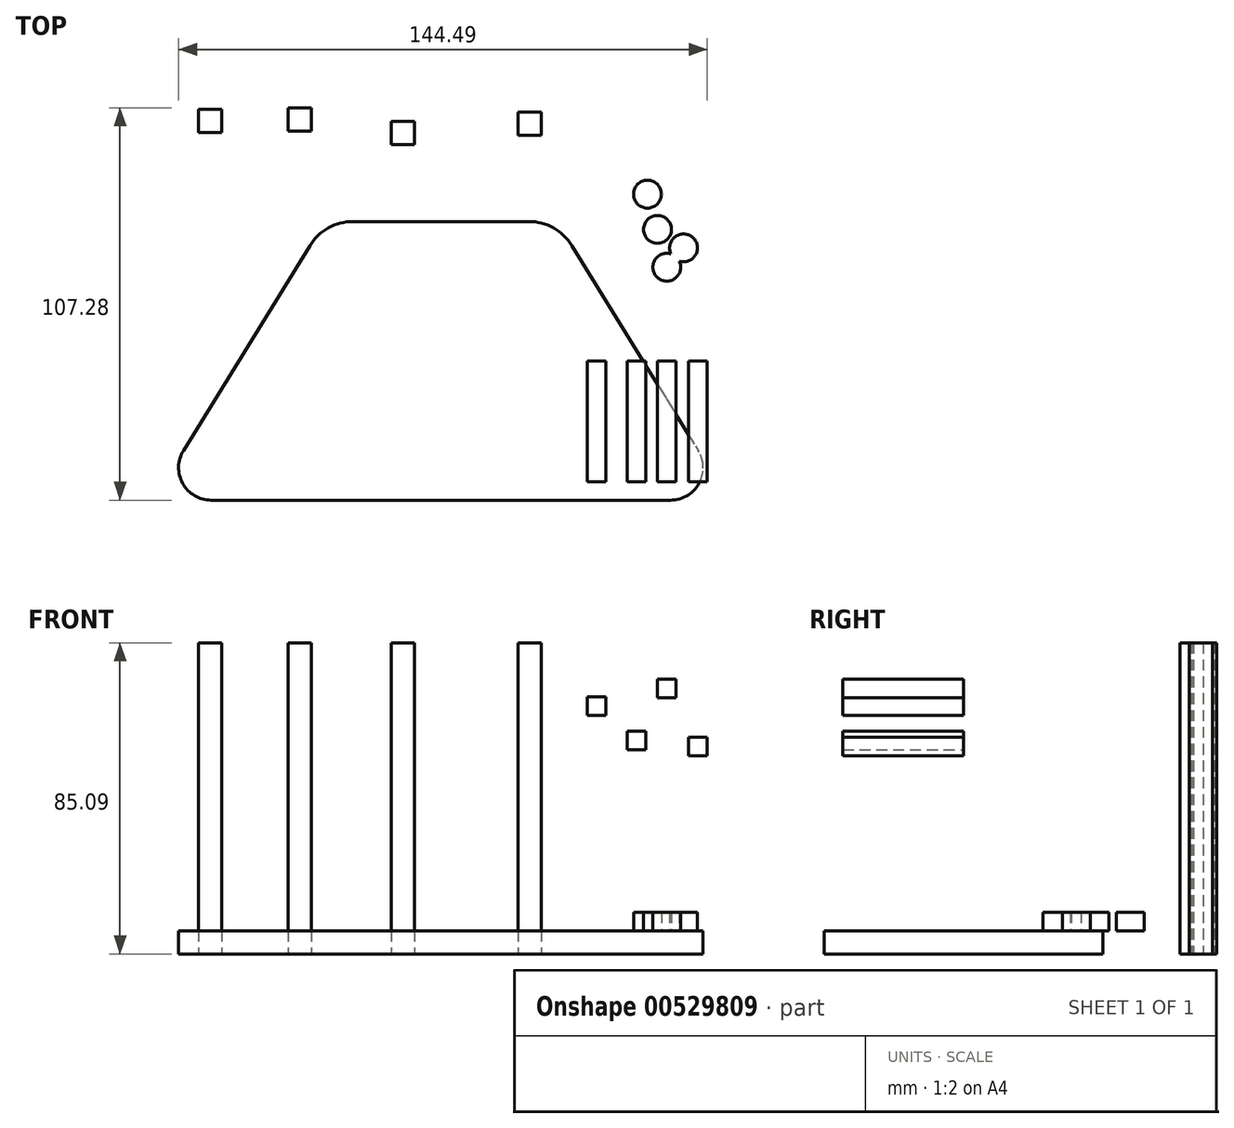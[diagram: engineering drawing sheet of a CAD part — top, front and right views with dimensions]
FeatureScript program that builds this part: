
annotation { "Feature Type Name" : "Feature", "Feature Type Description" : "" }
export const myFeature = defineFeature(function(context is Context, id is Id, definition is map)
    precondition{}
    {
        {
            var Q0;
            Q0=qCreatedBy(makeId("Top.planeOp"),FACE);
            var sketch = newSketch(context, id + "F0", { "sketchPlane" : qUnion([Q0])});
            skLineSegment(sketch, "E0.bottom", {"start": v(-23.95, 38.1) * mm, "end": v(23.95, 38.1) * mm});
            skLineSegment(sketch, "E0.top", {"start": v(-31.75, -38.1) * mm, "end": v(31.75, -38.1) * mm});
            skLineSegment(sketch, "E0.left", {"start": v(-31.75, 38.1) * mm, "end": v(-31.75, -38.1) * mm});
            skLineSegment(sketch, "E0.right", {"start": v(31.75, 38.1) * mm, "end": v(31.75, -38.1) * mm});
            skPoint(sketch, "E0.middle", {"position": v(0, 0) * mm});
            skLineSegment(sketch, "E1", {"start": v(-31.75, -38.1) * mm, "end": v(-62.81, -38.1) * mm});
            skLineSegment(sketch, "E2", {"start": v(31.75, -38.1) * mm, "end": v(62.81, -38.1) * mm});
            skLineSegment(sketch, "E3", {"start": v(-70.38, -24.54) * mm, "end": v(-35.84, 31.46) * mm});
            skLineSegment(sketch, "E4", {"start": v(35.84, 31.46) * mm, "end": v(70.38, -24.54) * mm});
            skPoint(sketch, "E5.visualSharp", {"position": v(-31.75, 38.1) * mm});
            skArc(sketch, "E5.filletArc", {"start": v(-23.95, 38.1) * mm, "mid": v(-30.76, 36.33) * mm, "end": v(-35.84, 31.46) * mm});
            skPoint(sketch, "E6.visualSharp", {"position": v(31.75, 38.1) * mm});
            skArc(sketch, "E6.filletArc", {"start": v(35.84, 31.46) * mm, "mid": v(30.76, 36.33) * mm, "end": v(23.95, 38.1) * mm});
            skPoint(sketch, "E7.visualSharp", {"position": v(78.74, -38.1) * mm});
            skArc(sketch, "E7.filletArc", {"start": v(62.81, -38.1) * mm, "mid": v(70.58, -33.54) * mm, "end": v(70.38, -24.54) * mm});
            skPoint(sketch, "E8.visualSharp", {"position": v(-78.74, -38.1) * mm});
            skArc(sketch, "E8.filletArc", {"start": v(-70.38, -24.54) * mm, "mid": v(-70.58, -33.54) * mm, "end": v(-62.81, -38.1) * mm});
            skSolve(sketch);
        }
        {
            var Q0;
            {var subQ7=sQuery(id+"F0.wireOp",EDGE,"E0.bottom");Q0=makeQuery(id+"F0.imprint","IMPRINT",FACE,{"disambiguationData":[TD([[makeQuery(id+"F0.imprint","IMPRINT",EDGE,{"derivedFrom":subQ7}),-1.0]])]});}
            var Q1;
            {var subQ4=sQuery(id+"F0.wireOp",EDGE,"E1");Q1=makeQuery(id+"F0.imprint","IMPRINT",FACE,{"disambiguationData":[TD([[makeQuery(id+"F0.imprint","IMPRINT",EDGE,{"derivedFrom":subQ4}),-1.0]])]});}
            var Q2;
            {var subQ4=sQuery(id+"F0.wireOp",EDGE,"E2");Q2=makeQuery(id+"F0.imprint","IMPRINT",FACE,{"disambiguationData":[TD([[makeQuery(id+"F0.imprint","IMPRINT",EDGE,{"derivedFrom":subQ4}),1.0]])]});}
            extrude(context, id + "F1", {"entities" : qUnion([Q0, Q1, Q2]), "depth" : 6.35 * mm, "offsetDistance" : 25.4 * mm});
        }
        {
            var Q0;
            Q0=qCreatedBy(makeId("Top.planeOp"),FACE);
            var sketch = newSketch(context, id + "F2", { "sketchPlane" : qUnion([Q0])});
            skLineSegment(sketch, "E9.bottom", {"start": v(-59.93, 62.37) * mm, "end": v(-66.28, 62.37) * mm});
            skLineSegment(sketch, "E9.top", {"start": v(-59.93, 68.72) * mm, "end": v(-66.28, 68.72) * mm});
            skLineSegment(sketch, "E9.left", {"start": v(-59.93, 62.37) * mm, "end": v(-59.93, 68.72) * mm});
            skLineSegment(sketch, "E9.right", {"start": v(-66.28, 62.37) * mm, "end": v(-66.28, 68.72) * mm});
            skPoint(sketch, "E9.middle", {"position": v(-63.1, 65.55) * mm});
            skLineSegment(sketch, "E10.bottom", {"start": v(-35.4, 62.83) * mm, "end": v(-41.75, 62.83) * mm});
            skLineSegment(sketch, "E10.top", {"start": v(-35.4, 69.18) * mm, "end": v(-41.75, 69.18) * mm});
            skLineSegment(sketch, "E10.left", {"start": v(-35.4, 62.83) * mm, "end": v(-35.4, 69.18) * mm});
            skLineSegment(sketch, "E10.right", {"start": v(-41.75, 62.83) * mm, "end": v(-41.75, 69.18) * mm});
            skPoint(sketch, "E10.middle", {"position": v(-38.57, 66) * mm});
            skLineSegment(sketch, "E11.bottom", {"start": v(-7.16, 59.16) * mm, "end": v(-13.5, 59.16) * mm});
            skLineSegment(sketch, "E11.top", {"start": v(-7.16, 65.5) * mm, "end": v(-13.5, 65.5) * mm});
            skLineSegment(sketch, "E11.left", {"start": v(-7.16, 59.16) * mm, "end": v(-7.16, 65.5) * mm});
            skLineSegment(sketch, "E11.right", {"start": v(-13.5, 59.16) * mm, "end": v(-13.5, 65.5) * mm});
            skPoint(sketch, "E11.middle", {"position": v(-10.33, 62.33) * mm});
            skLineSegment(sketch, "E12.bottom", {"start": v(27.51, 61.68) * mm, "end": v(21.16, 61.68) * mm});
            skLineSegment(sketch, "E12.top", {"start": v(27.51, 68.03) * mm, "end": v(21.16, 68.03) * mm});
            skLineSegment(sketch, "E12.left", {"start": v(27.51, 61.68) * mm, "end": v(27.51, 68.03) * mm});
            skLineSegment(sketch, "E12.right", {"start": v(21.16, 61.68) * mm, "end": v(21.16, 68.03) * mm});
            skPoint(sketch, "E12.middle", {"position": v(24.34, 64.86) * mm});
            skSolve(sketch);
        }
        {
            var Q0;
            Q0=makeQuery(id+"F2.imprint","IMPRINT",FACE,{"disambiguationData":[TD([[makeQuery(id+"F2.imprint","IMPRINT",EDGE,{"derivedFrom":sQuery(id+"F2.wireOp",EDGE,"E11.bottom")}),-1.0]])]});
            var Q1;
            Q1=makeQuery(id+"F2.imprint","IMPRINT",FACE,{"disambiguationData":[TD([[makeQuery(id+"F2.imprint","IMPRINT",EDGE,{"derivedFrom":sQuery(id+"F2.wireOp",EDGE,"E12.bottom")}),-1.0]])]});
            var Q2;
            Q2=makeQuery(id+"F2.imprint","IMPRINT",FACE,{"disambiguationData":[TD([[makeQuery(id+"F2.imprint","IMPRINT",EDGE,{"derivedFrom":sQuery(id+"F2.wireOp",EDGE,"E9.bottom")}),-1.0]])]});
            var Q3;
            Q3=makeQuery(id+"F2.imprint","IMPRINT",FACE,{"disambiguationData":[TD([[makeQuery(id+"F2.imprint","IMPRINT",EDGE,{"derivedFrom":sQuery(id+"F2.wireOp",EDGE,"E10.bottom")}),-1.0]])]});
            extrude(context, id + "F3", {"entities" : qUnion([Q0, Q1, Q2, Q3]), "depth" : 85.1 * mm, "offsetDistance" : 25.4 * mm});
        }
        {
            var Q0;
            Q0=qCreatedBy(makeId("Front.planeOp"),FACE);
            var sketch = newSketch(context, id + "F4", { "sketchPlane" : qUnion([Q0])});
            skLineSegment(sketch, "E13.bottom", {"start": v(45.11, 65.23) * mm, "end": v(40.03, 65.23) * mm});
            skLineSegment(sketch, "E13.top", {"start": v(45.11, 70.3) * mm, "end": v(40.03, 70.3) * mm});
            skLineSegment(sketch, "E13.left", {"start": v(45.11, 65.23) * mm, "end": v(45.11, 70.3) * mm});
            skLineSegment(sketch, "E13.right", {"start": v(40.03, 65.23) * mm, "end": v(40.03, 70.3) * mm});
            skPoint(sketch, "E13.middle", {"position": v(42.57, 67.77) * mm});
            skLineSegment(sketch, "E14.bottom", {"start": v(56.03, 55.8) * mm, "end": v(50.95, 55.8) * mm});
            skLineSegment(sketch, "E14.top", {"start": v(56.03, 60.89) * mm, "end": v(50.95, 60.89) * mm});
            skLineSegment(sketch, "E14.left", {"start": v(56.03, 55.8) * mm, "end": v(56.03, 60.89) * mm});
            skLineSegment(sketch, "E14.right", {"start": v(50.95, 55.8) * mm, "end": v(50.95, 60.89) * mm});
            skPoint(sketch, "E14.middle", {"position": v(53.5, 58.35) * mm});
            skLineSegment(sketch, "E15.bottom", {"start": v(64.3, 70.1) * mm, "end": v(59.22, 70.1) * mm});
            skLineSegment(sketch, "E15.top", {"start": v(64.3, 75.18) * mm, "end": v(59.22, 75.18) * mm});
            skLineSegment(sketch, "E15.left", {"start": v(64.3, 70.1) * mm, "end": v(64.3, 75.18) * mm});
            skLineSegment(sketch, "E15.right", {"start": v(59.22, 70.1) * mm, "end": v(59.22, 75.18) * mm});
            skPoint(sketch, "E15.middle", {"position": v(61.76, 72.64) * mm});
            skLineSegment(sketch, "E16.bottom", {"start": v(72.8, 54.19) * mm, "end": v(67.71, 54.19) * mm});
            skLineSegment(sketch, "E16.top", {"start": v(72.8, 59.27) * mm, "end": v(67.71, 59.27) * mm});
            skLineSegment(sketch, "E16.left", {"start": v(72.8, 54.19) * mm, "end": v(72.8, 59.27) * mm});
            skLineSegment(sketch, "E16.right", {"start": v(67.71, 54.19) * mm, "end": v(67.71, 59.27) * mm});
            skPoint(sketch, "E16.middle", {"position": v(70.25, 56.73) * mm});
            skSolve(sketch);
        }
        {
            var Q0;
            Q0=makeQuery(id+"F1.opExtrude","CAP_FACE",FACE,{"disambiguationData":[OSD([sQuery(id+"F0.wireOp",EDGE,"E0.bottom"),sQuery(id+"F0.wireOp",EDGE,"E0.top"),sQuery(id+"F0.wireOp",EDGE,"E1"),sQuery(id+"F0.wireOp",EDGE,"E2"),sQuery(id+"F0.wireOp",EDGE,"E3"),sQuery(id+"F0.wireOp",EDGE,"E4"),sQuery(id+"F0.wireOp",EDGE,"E5.filletArc"),sQuery(id+"F0.wireOp",EDGE,"E6.filletArc"),sQuery(id+"F0.wireOp",EDGE,"E7.filletArc"),sQuery(id+"F0.wireOp",EDGE,"E8.filletArc")])],"isStart":false});
            var sketch = newSketch(context, id + "F5", { "sketchPlane" : qUnion([Q0])});
            skCircle(sketch, "E17", {"center": v(56.48, 45.57) * mm, "radius": 3.81 * mm});
            skCircle(sketch, "E18", {"center": v(59.23, 35.93) * mm, "radius": 3.81 * mm});
            skCircle(sketch, "E19", {"center": v(66.35, 30.88) * mm, "radius": 3.81 * mm});
            skCircle(sketch, "E20", {"center": v(61.76, 25.6) * mm, "radius": 3.81 * mm});
            skSolve(sketch);
        }
        {
            var Q0;
            Q0 = qSketchRegion(id + "F5", true);
            var Q1;
            Q1=makeQuery(id+"F5.imprint","IMPRINT",FACE,{"disambiguationData":[TD([[makeQuery(id+"F5.imprint","IMPRINT",EDGE,{"derivedFrom":sQuery(id+"F5.wireOp",EDGE,"E17")}),1.0]])]});
            var Q2;
            Q2=makeQuery(id+"F5.imprint","IMPRINT",FACE,{"disambiguationData":[TD([[makeQuery(id+"F5.imprint","IMPRINT",EDGE,{"derivedFrom":sQuery(id+"F5.wireOp",EDGE,"E18")}),1.0]])]});
            var Q3;
            {var subQ0=sQuery(id+"F5.wireOp",EDGE,"E20");var subQ1=sQuery(id+"F5.wireOp",EDGE,"E19");var subQ2=makeQuery(id+"F5.imprint","INTERSECT",VERTEX,{"disambiguationData":[OD(0.0)],"derivedFrom":[subQ1,subQ0]});Q3=makeQuery(id+"F5.imprint","IMPRINT",FACE,{"disambiguationData":[TD([[makeQuery(id+"F5.imprint","IMPRINT",EDGE,{"disambiguationData":[TD([[subQ2,-1.0]])],"derivedFrom":subQ1}),-1.0]])]});}
            var Q4;
            {var subQ0=sQuery(id+"F5.wireOp",EDGE,"E20");var subQ1=sQuery(id+"F5.wireOp",EDGE,"E19");var subQ2=makeQuery(id+"F5.imprint","INTERSECT",VERTEX,{"disambiguationData":[OD(0.0)],"derivedFrom":[subQ1,subQ0]});Q4=makeQuery(id+"F5.imprint","IMPRINT",FACE,{"disambiguationData":[TD([[makeQuery(id+"F5.imprint","IMPRINT",EDGE,{"disambiguationData":[TD([[subQ2,1.0]])],"derivedFrom":subQ1}),1.0]])]});}
            var Q5;
            {var subQ0=sQuery(id+"F5.wireOp",EDGE,"E20");var subQ1=sQuery(id+"F5.wireOp",EDGE,"E19");var subQ2=makeQuery(id+"F5.imprint","INTERSECT",VERTEX,{"disambiguationData":[OD(0.0)],"derivedFrom":[subQ1,subQ0]});Q5=makeQuery(id+"F5.imprint","IMPRINT",FACE,{"disambiguationData":[TD([[makeQuery(id+"F5.imprint","IMPRINT",EDGE,{"disambiguationData":[TD([[subQ2,-1.0]])],"derivedFrom":subQ1}),1.0]])]});}
            extrude(context, id + "F6", {"entities" : qUnion([Q0, Q1, Q2, Q3, Q4, Q5]), "depth" : 5.08 * mm, "offsetDistance" : 25.4 * mm});
        }
        {
            var Q0;
            Q0=makeQuery(id+"F4.imprint","IMPRINT",FACE,{"disambiguationData":[TD([[makeQuery(id+"F4.imprint","IMPRINT",EDGE,{"derivedFrom":sQuery(id+"F4.wireOp",EDGE,"E13.bottom")}),-1.0]])]});
            var Q1;
            Q1=makeQuery(id+"F4.imprint","IMPRINT",FACE,{"disambiguationData":[TD([[makeQuery(id+"F4.imprint","IMPRINT",EDGE,{"derivedFrom":sQuery(id+"F4.wireOp",EDGE,"E14.bottom")}),-1.0]])]});
            var Q2;
            Q2=makeQuery(id+"F4.imprint","IMPRINT",FACE,{"disambiguationData":[TD([[makeQuery(id+"F4.imprint","IMPRINT",EDGE,{"derivedFrom":sQuery(id+"F4.wireOp",EDGE,"E16.bottom")}),-1.0]])]});
            var Q3;
            Q3=makeQuery(id+"F4.imprint","IMPRINT",FACE,{"disambiguationData":[TD([[makeQuery(id+"F4.imprint","IMPRINT",EDGE,{"derivedFrom":sQuery(id+"F4.wireOp",EDGE,"E15.bottom")}),-1.0]])]});
            extrude(context, id + "F7", {"entities" : qUnion([Q0, Q1, Q2, Q3]), "depth" : 33.02 * mm, "offsetDistance" : 25.4 * mm});
        }
    });
